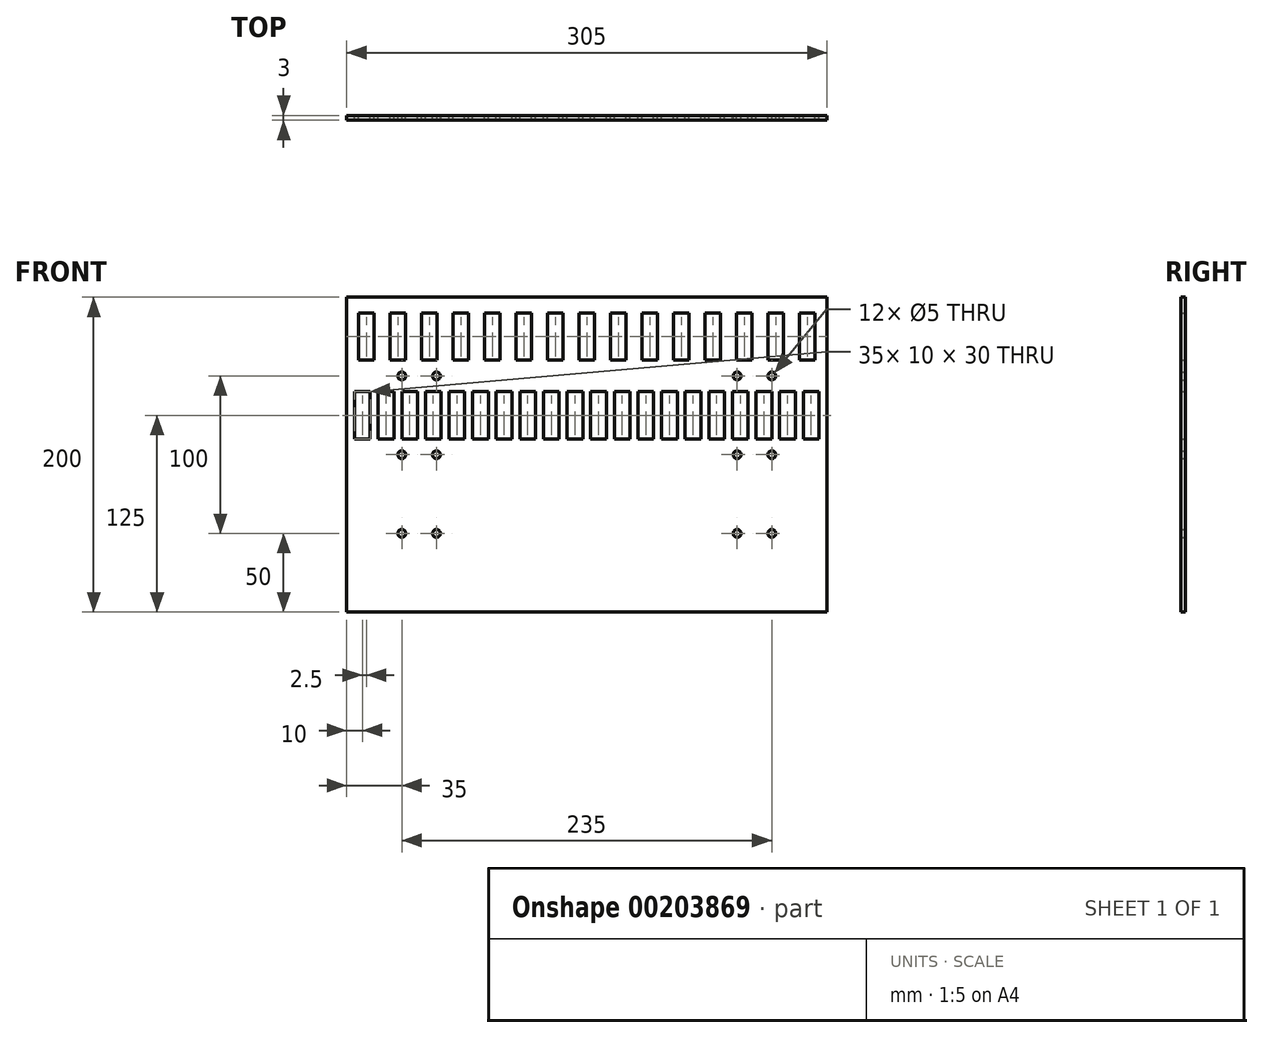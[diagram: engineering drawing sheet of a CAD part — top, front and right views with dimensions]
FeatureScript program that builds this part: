
annotation { "Feature Type Name" : "Feature", "Feature Type Description" : "" }
export const myFeature = defineFeature(function(context is Context, id is Id, definition is map)
    precondition{}
    {
        {
            var Q0;
            Q0=qCreatedBy(makeId("Front.planeOp"),FACE);
            var sketch = newSketch(context, id + "F0", { "sketchPlane" : qUnion([Q0])});
            skLineSegment(sketch, "E0.left", {"start": v(-147.5, 40) * mm, "end": v(-147.5, 10) * mm});
            skLineSegment(sketch, "E0.right", {"start": v(-137.5, 40) * mm, "end": v(-137.5, 10) * mm});
            skLineSegment(sketch, "E1", {"start": v(0, 0) * mm, "end": v(-152.5, 0) * mm, "construction": true});
            skLineSegment(sketch, "E2", {"start": v(-137.5, 40) * mm, "end": v(-147.5, 40) * mm});
            skLineSegment(sketch, "E3", {"start": v(-147.5, 10) * mm, "end": v(-137.5, 10) * mm});
            skLineSegment(sketch, "E4", {"start": v(0, 0) * mm, "end": v(0, 100) * mm, "construction": true});
            skLineSegment(sketch, "E5.bottom", {"start": v(-152.5, -100) * mm, "end": v(152.5, -100) * mm});
            skLineSegment(sketch, "E5.top", {"start": v(-152.5, 100) * mm, "end": v(152.5, 100) * mm});
            skLineSegment(sketch, "E5.left", {"start": v(-152.5, -100) * mm, "end": v(-152.5, 100) * mm});
            skLineSegment(sketch, "E5.right", {"start": v(152.5, -100) * mm, "end": v(152.5, 100) * mm});
            skLineSegment(sketch, "E6.1.0.0", {"start": v(-132.5, 10) * mm, "end": v(-122.5, 10) * mm});
            skLineSegment(sketch, "E6.1.0.1", {"start": v(-122.5, 40) * mm, "end": v(-132.5, 40) * mm});
            skLineSegment(sketch, "E6.1.0.2", {"start": v(-122.5, 40) * mm, "end": v(-122.5, 10) * mm});
            skLineSegment(sketch, "E6.1.0.3", {"start": v(-132.5, 40) * mm, "end": v(-132.5, 10) * mm});
            skLineSegment(sketch, "E6.2.0.0", {"start": v(-117.5, 10) * mm, "end": v(-107.5, 10) * mm});
            skLineSegment(sketch, "E6.2.0.1", {"start": v(-107.5, 40) * mm, "end": v(-117.5, 40) * mm});
            skLineSegment(sketch, "E6.2.0.2", {"start": v(-107.5, 40) * mm, "end": v(-107.5, 10) * mm});
            skLineSegment(sketch, "E6.2.0.3", {"start": v(-117.5, 40) * mm, "end": v(-117.5, 10) * mm});
            skLineSegment(sketch, "E6.3.0.0", {"start": v(-102.5, 10) * mm, "end": v(-92.5, 10) * mm});
            skLineSegment(sketch, "E6.3.0.1", {"start": v(-92.5, 40) * mm, "end": v(-102.5, 40) * mm});
            skLineSegment(sketch, "E6.3.0.2", {"start": v(-92.5, 40) * mm, "end": v(-92.5, 10) * mm});
            skLineSegment(sketch, "E6.3.0.3", {"start": v(-102.5, 40) * mm, "end": v(-102.5, 10) * mm});
            skLineSegment(sketch, "E6.4.0.0", {"start": v(-87.5, 10) * mm, "end": v(-77.5, 10) * mm});
            skLineSegment(sketch, "E6.4.0.1", {"start": v(-77.5, 40) * mm, "end": v(-87.5, 40) * mm});
            skLineSegment(sketch, "E6.4.0.2", {"start": v(-77.5, 40) * mm, "end": v(-77.5, 10) * mm});
            skLineSegment(sketch, "E6.4.0.3", {"start": v(-87.5, 40) * mm, "end": v(-87.5, 10) * mm});
            skLineSegment(sketch, "E6.5.0.0", {"start": v(-72.5, 10) * mm, "end": v(-62.5, 10) * mm});
            skLineSegment(sketch, "E6.5.0.1", {"start": v(-62.5, 40) * mm, "end": v(-72.5, 40) * mm});
            skLineSegment(sketch, "E6.5.0.2", {"start": v(-62.5, 40) * mm, "end": v(-62.5, 10) * mm});
            skLineSegment(sketch, "E6.5.0.3", {"start": v(-72.5, 40) * mm, "end": v(-72.5, 10) * mm});
            skLineSegment(sketch, "E6.6.0.0", {"start": v(-57.5, 10) * mm, "end": v(-47.5, 10) * mm});
            skLineSegment(sketch, "E6.6.0.1", {"start": v(-47.5, 40) * mm, "end": v(-57.5, 40) * mm});
            skLineSegment(sketch, "E6.6.0.2", {"start": v(-47.5, 40) * mm, "end": v(-47.5, 10) * mm});
            skLineSegment(sketch, "E6.6.0.3", {"start": v(-57.5, 40) * mm, "end": v(-57.5, 10) * mm});
            skLineSegment(sketch, "E6.7.0.0", {"start": v(-42.5, 10) * mm, "end": v(-32.5, 10) * mm});
            skLineSegment(sketch, "E6.7.0.1", {"start": v(-32.5, 40) * mm, "end": v(-42.5, 40) * mm});
            skLineSegment(sketch, "E6.7.0.2", {"start": v(-32.5, 40) * mm, "end": v(-32.5, 10) * mm});
            skLineSegment(sketch, "E6.7.0.3", {"start": v(-42.5, 40) * mm, "end": v(-42.5, 10) * mm});
            skLineSegment(sketch, "E6.8.0.0", {"start": v(-27.5, 10) * mm, "end": v(-17.5, 10) * mm});
            skLineSegment(sketch, "E6.8.0.1", {"start": v(-17.5, 40) * mm, "end": v(-27.5, 40) * mm});
            skLineSegment(sketch, "E6.8.0.2", {"start": v(-17.5, 40) * mm, "end": v(-17.5, 10) * mm});
            skLineSegment(sketch, "E6.8.0.3", {"start": v(-27.5, 40) * mm, "end": v(-27.5, 10) * mm});
            skLineSegment(sketch, "E6.9.0.0", {"start": v(-12.5, 10) * mm, "end": v(-2.5, 10) * mm});
            skLineSegment(sketch, "E6.9.0.1", {"start": v(-2.5, 40) * mm, "end": v(-12.5, 40) * mm});
            skLineSegment(sketch, "E6.9.0.2", {"start": v(-2.5, 40) * mm, "end": v(-2.5, 10) * mm});
            skLineSegment(sketch, "E6.9.0.3", {"start": v(-12.5, 40) * mm, "end": v(-12.5, 10) * mm});
            skLineSegment(sketch, "E6.10.0.0", {"start": v(2.5, 10) * mm, "end": v(12.5, 10) * mm});
            skLineSegment(sketch, "E6.10.0.1", {"start": v(12.5, 40) * mm, "end": v(2.5, 40) * mm});
            skLineSegment(sketch, "E6.10.0.2", {"start": v(12.5, 40) * mm, "end": v(12.5, 10) * mm});
            skLineSegment(sketch, "E6.10.0.3", {"start": v(2.5, 40) * mm, "end": v(2.5, 10) * mm});
            skLineSegment(sketch, "E6.11.0.0", {"start": v(17.5, 10) * mm, "end": v(27.5, 10) * mm});
            skLineSegment(sketch, "E6.11.0.1", {"start": v(27.5, 40) * mm, "end": v(17.5, 40) * mm});
            skLineSegment(sketch, "E6.11.0.2", {"start": v(27.5, 40) * mm, "end": v(27.5, 10) * mm});
            skLineSegment(sketch, "E6.11.0.3", {"start": v(17.5, 40) * mm, "end": v(17.5, 10) * mm});
            skLineSegment(sketch, "E6.12.0.0", {"start": v(32.5, 10) * mm, "end": v(42.5, 10) * mm});
            skLineSegment(sketch, "E6.12.0.1", {"start": v(42.5, 40) * mm, "end": v(32.5, 40) * mm});
            skLineSegment(sketch, "E6.12.0.2", {"start": v(42.5, 40) * mm, "end": v(42.5, 10) * mm});
            skLineSegment(sketch, "E6.12.0.3", {"start": v(32.5, 40) * mm, "end": v(32.5, 10) * mm});
            skLineSegment(sketch, "E6.13.0.0", {"start": v(47.5, 10) * mm, "end": v(57.5, 10) * mm});
            skLineSegment(sketch, "E6.13.0.1", {"start": v(57.5, 40) * mm, "end": v(47.5, 40) * mm});
            skLineSegment(sketch, "E6.13.0.2", {"start": v(57.5, 40) * mm, "end": v(57.5, 10) * mm});
            skLineSegment(sketch, "E6.13.0.3", {"start": v(47.5, 40) * mm, "end": v(47.5, 10) * mm});
            skLineSegment(sketch, "E6.14.0.0", {"start": v(62.5, 10) * mm, "end": v(72.5, 10) * mm});
            skLineSegment(sketch, "E6.14.0.1", {"start": v(72.5, 40) * mm, "end": v(62.5, 40) * mm});
            skLineSegment(sketch, "E6.14.0.2", {"start": v(72.5, 40) * mm, "end": v(72.5, 10) * mm});
            skLineSegment(sketch, "E6.14.0.3", {"start": v(62.5, 40) * mm, "end": v(62.5, 10) * mm});
            skLineSegment(sketch, "E6.15.0.0", {"start": v(77.5, 10) * mm, "end": v(87.5, 10) * mm});
            skLineSegment(sketch, "E6.15.0.1", {"start": v(87.5, 40) * mm, "end": v(77.5, 40) * mm});
            skLineSegment(sketch, "E6.15.0.2", {"start": v(87.5, 40) * mm, "end": v(87.5, 10) * mm});
            skLineSegment(sketch, "E6.15.0.3", {"start": v(77.5, 40) * mm, "end": v(77.5, 10) * mm});
            skLineSegment(sketch, "E6.16.0.0", {"start": v(92.5, 10) * mm, "end": v(102.5, 10) * mm});
            skLineSegment(sketch, "E6.16.0.1", {"start": v(102.5, 40) * mm, "end": v(92.5, 40) * mm});
            skLineSegment(sketch, "E6.16.0.2", {"start": v(102.5, 40) * mm, "end": v(102.5, 10) * mm});
            skLineSegment(sketch, "E6.16.0.3", {"start": v(92.5, 40) * mm, "end": v(92.5, 10) * mm});
            skLineSegment(sketch, "E6.17.0.0", {"start": v(107.5, 10) * mm, "end": v(117.5, 10) * mm});
            skLineSegment(sketch, "E6.17.0.1", {"start": v(117.5, 40) * mm, "end": v(107.5, 40) * mm});
            skLineSegment(sketch, "E6.17.0.2", {"start": v(117.5, 40) * mm, "end": v(117.5, 10) * mm});
            skLineSegment(sketch, "E6.17.0.3", {"start": v(107.5, 40) * mm, "end": v(107.5, 10) * mm});
            skLineSegment(sketch, "E6.18.0.0", {"start": v(122.5, 10) * mm, "end": v(132.5, 10) * mm});
            skLineSegment(sketch, "E6.18.0.1", {"start": v(132.5, 40) * mm, "end": v(122.5, 40) * mm});
            skLineSegment(sketch, "E6.18.0.2", {"start": v(132.5, 40) * mm, "end": v(132.5, 10) * mm});
            skLineSegment(sketch, "E6.18.0.3", {"start": v(122.5, 40) * mm, "end": v(122.5, 10) * mm});
            skLineSegment(sketch, "E6.19.0.0", {"start": v(137.5, 10) * mm, "end": v(147.5, 10) * mm});
            skLineSegment(sketch, "E6.19.0.1", {"start": v(147.5, 40) * mm, "end": v(137.5, 40) * mm});
            skLineSegment(sketch, "E6.19.0.2", {"start": v(147.5, 40) * mm, "end": v(147.5, 10) * mm});
            skLineSegment(sketch, "E6.19.0.3", {"start": v(137.5, 40) * mm, "end": v(137.5, 10) * mm});
            skLineSegment(sketch, "E6.direction1", {"start": v(-147.5, 10) * mm, "end": v(-132.5, 10) * mm, "construction": true});
            skCircle(sketch, "E7", {"center": v(-117.5, 0) * mm, "radius": 2.5 * mm});
            skCircle(sketch, "E8", {"center": v(-95.5, 0) * mm, "radius": 2.5 * mm});
            skLineSegment(sketch, "E9", {"start": v(1.56, 0) * mm, "end": v(152.5, 0) * mm, "construction": true});
            skCircle(sketch, "E10", {"center": v(117.5, 0) * mm, "radius": 2.5 * mm});
            skCircle(sketch, "E11", {"center": v(95.5, 0) * mm, "radius": 2.5 * mm});
            skLineSegment(sketch, "E12", {"start": v(-152.5, 50) * mm, "end": v(152.5, 50) * mm, "construction": true});
            skLineSegment(sketch, "E13", {"start": v(-152.5, -50) * mm, "end": v(152.5, -50) * mm, "construction": true});
            skCircle(sketch, "E14", {"center": v(-117.5, 50) * mm, "radius": 2.5 * mm});
            skCircle(sketch, "E15", {"center": v(-95.5, 50) * mm, "radius": 2.5 * mm});
            skCircle(sketch, "E16", {"center": v(117.5, 50) * mm, "radius": 2.5 * mm});
            skCircle(sketch, "E17", {"center": v(95.5, 50) * mm, "radius": 2.5 * mm});
            skCircle(sketch, "E18", {"center": v(-117.5, -50) * mm, "radius": 2.5 * mm});
            skCircle(sketch, "E19", {"center": v(-95.5, -50) * mm, "radius": 2.5 * mm});
            skCircle(sketch, "E20", {"center": v(95.5, -50) * mm, "radius": 2.5 * mm});
            skCircle(sketch, "E21", {"center": v(117.5, -50) * mm, "radius": 2.5 * mm});
            skLineSegment(sketch, "E22.bottom", {"start": v(-145, 90) * mm, "end": v(-135, 90) * mm});
            skLineSegment(sketch, "E22.top", {"start": v(-145, 60) * mm, "end": v(-135, 60) * mm});
            skLineSegment(sketch, "E22.left", {"start": v(-145, 90) * mm, "end": v(-145, 60) * mm});
            skLineSegment(sketch, "E22.right", {"start": v(-135, 90) * mm, "end": v(-135, 60) * mm});
            skLineSegment(sketch, "E23.1.0.0", {"start": v(-115, 90) * mm, "end": v(-115, 60) * mm});
            skLineSegment(sketch, "E23.1.0.1", {"start": v(-125, 90) * mm, "end": v(-115, 90) * mm});
            skLineSegment(sketch, "E23.1.0.2", {"start": v(-125, 90) * mm, "end": v(-125, 60) * mm});
            skLineSegment(sketch, "E23.1.0.3", {"start": v(-125, 60) * mm, "end": v(-115, 60) * mm});
            skLineSegment(sketch, "E23.2.0.0", {"start": v(-95, 90) * mm, "end": v(-95, 60) * mm});
            skLineSegment(sketch, "E23.2.0.1", {"start": v(-105, 90) * mm, "end": v(-95, 90) * mm});
            skLineSegment(sketch, "E23.2.0.2", {"start": v(-105, 90) * mm, "end": v(-105, 60) * mm});
            skLineSegment(sketch, "E23.2.0.3", {"start": v(-105, 60) * mm, "end": v(-95, 60) * mm});
            skLineSegment(sketch, "E23.3.0.0", {"start": v(-75, 90) * mm, "end": v(-75, 60) * mm});
            skLineSegment(sketch, "E23.3.0.1", {"start": v(-85, 90) * mm, "end": v(-75, 90) * mm});
            skLineSegment(sketch, "E23.3.0.2", {"start": v(-85, 90) * mm, "end": v(-85, 60) * mm});
            skLineSegment(sketch, "E23.3.0.3", {"start": v(-85, 60) * mm, "end": v(-75, 60) * mm});
            skLineSegment(sketch, "E23.4.0.0", {"start": v(-55, 90) * mm, "end": v(-55, 60) * mm});
            skLineSegment(sketch, "E23.4.0.1", {"start": v(-65, 90) * mm, "end": v(-55, 90) * mm});
            skLineSegment(sketch, "E23.4.0.2", {"start": v(-65, 90) * mm, "end": v(-65, 60) * mm});
            skLineSegment(sketch, "E23.4.0.3", {"start": v(-65, 60) * mm, "end": v(-55, 60) * mm});
            skLineSegment(sketch, "E23.5.0.0", {"start": v(-35, 90) * mm, "end": v(-35, 60) * mm});
            skLineSegment(sketch, "E23.5.0.1", {"start": v(-45, 90) * mm, "end": v(-35, 90) * mm});
            skLineSegment(sketch, "E23.5.0.2", {"start": v(-45, 90) * mm, "end": v(-45, 60) * mm});
            skLineSegment(sketch, "E23.5.0.3", {"start": v(-45, 60) * mm, "end": v(-35, 60) * mm});
            skLineSegment(sketch, "E23.6.0.0", {"start": v(-15, 90) * mm, "end": v(-15, 60) * mm});
            skLineSegment(sketch, "E23.6.0.1", {"start": v(-25, 90) * mm, "end": v(-15, 90) * mm});
            skLineSegment(sketch, "E23.6.0.2", {"start": v(-25, 90) * mm, "end": v(-25, 60) * mm});
            skLineSegment(sketch, "E23.6.0.3", {"start": v(-25, 60) * mm, "end": v(-15, 60) * mm});
            skLineSegment(sketch, "E23.7.0.0", {"start": v(5, 90) * mm, "end": v(5, 60) * mm});
            skLineSegment(sketch, "E23.7.0.1", {"start": v(-5, 90) * mm, "end": v(5, 90) * mm});
            skLineSegment(sketch, "E23.7.0.2", {"start": v(-5, 90) * mm, "end": v(-5, 60) * mm});
            skLineSegment(sketch, "E23.7.0.3", {"start": v(-5, 60) * mm, "end": v(5, 60) * mm});
            skLineSegment(sketch, "E23.8.0.0", {"start": v(25, 90) * mm, "end": v(25, 60) * mm});
            skLineSegment(sketch, "E23.8.0.1", {"start": v(15, 90) * mm, "end": v(25, 90) * mm});
            skLineSegment(sketch, "E23.8.0.2", {"start": v(15, 90) * mm, "end": v(15, 60) * mm});
            skLineSegment(sketch, "E23.8.0.3", {"start": v(15, 60) * mm, "end": v(25, 60) * mm});
            skLineSegment(sketch, "E23.9.0.0", {"start": v(45, 90) * mm, "end": v(45, 60) * mm});
            skLineSegment(sketch, "E23.9.0.1", {"start": v(35, 90) * mm, "end": v(45, 90) * mm});
            skLineSegment(sketch, "E23.9.0.2", {"start": v(35, 90) * mm, "end": v(35, 60) * mm});
            skLineSegment(sketch, "E23.9.0.3", {"start": v(35, 60) * mm, "end": v(45, 60) * mm});
            skLineSegment(sketch, "E23.10.0.0", {"start": v(65, 90) * mm, "end": v(65, 60) * mm});
            skLineSegment(sketch, "E23.10.0.1", {"start": v(55, 90) * mm, "end": v(65, 90) * mm});
            skLineSegment(sketch, "E23.10.0.2", {"start": v(55, 90) * mm, "end": v(55, 60) * mm});
            skLineSegment(sketch, "E23.10.0.3", {"start": v(55, 60) * mm, "end": v(65, 60) * mm});
            skLineSegment(sketch, "E23.11.0.0", {"start": v(85, 90) * mm, "end": v(85, 60) * mm});
            skLineSegment(sketch, "E23.11.0.1", {"start": v(75, 90) * mm, "end": v(85, 90) * mm});
            skLineSegment(sketch, "E23.11.0.2", {"start": v(75, 90) * mm, "end": v(75, 60) * mm});
            skLineSegment(sketch, "E23.11.0.3", {"start": v(75, 60) * mm, "end": v(85, 60) * mm});
            skLineSegment(sketch, "E23.12.0.0", {"start": v(105, 90) * mm, "end": v(105, 60) * mm});
            skLineSegment(sketch, "E23.12.0.1", {"start": v(95, 90) * mm, "end": v(105, 90) * mm});
            skLineSegment(sketch, "E23.12.0.2", {"start": v(95, 90) * mm, "end": v(95, 60) * mm});
            skLineSegment(sketch, "E23.12.0.3", {"start": v(95, 60) * mm, "end": v(105, 60) * mm});
            skLineSegment(sketch, "E23.13.0.0", {"start": v(125, 90) * mm, "end": v(125, 60) * mm});
            skLineSegment(sketch, "E23.13.0.1", {"start": v(115, 90) * mm, "end": v(125, 90) * mm});
            skLineSegment(sketch, "E23.13.0.2", {"start": v(115, 90) * mm, "end": v(115, 60) * mm});
            skLineSegment(sketch, "E23.13.0.3", {"start": v(115, 60) * mm, "end": v(125, 60) * mm});
            skLineSegment(sketch, "E23.14.0.0", {"start": v(145, 90) * mm, "end": v(145, 60) * mm});
            skLineSegment(sketch, "E23.14.0.1", {"start": v(135, 90) * mm, "end": v(145, 90) * mm});
            skLineSegment(sketch, "E23.14.0.2", {"start": v(135, 90) * mm, "end": v(135, 60) * mm});
            skLineSegment(sketch, "E23.14.0.3", {"start": v(135, 60) * mm, "end": v(145, 60) * mm});
            skLineSegment(sketch, "E23.direction1", {"start": v(-135, 60) * mm, "end": v(-115, 60) * mm, "construction": true});
            skSolve(sketch);
        }
        {
            var Q0;
            Q0 = qSketchRegion(id + "F0", true);
            extrude(context, id + "F1", {"entities" : qUnion([Q0]), "depth" : 3 * mm});
        }
    });
